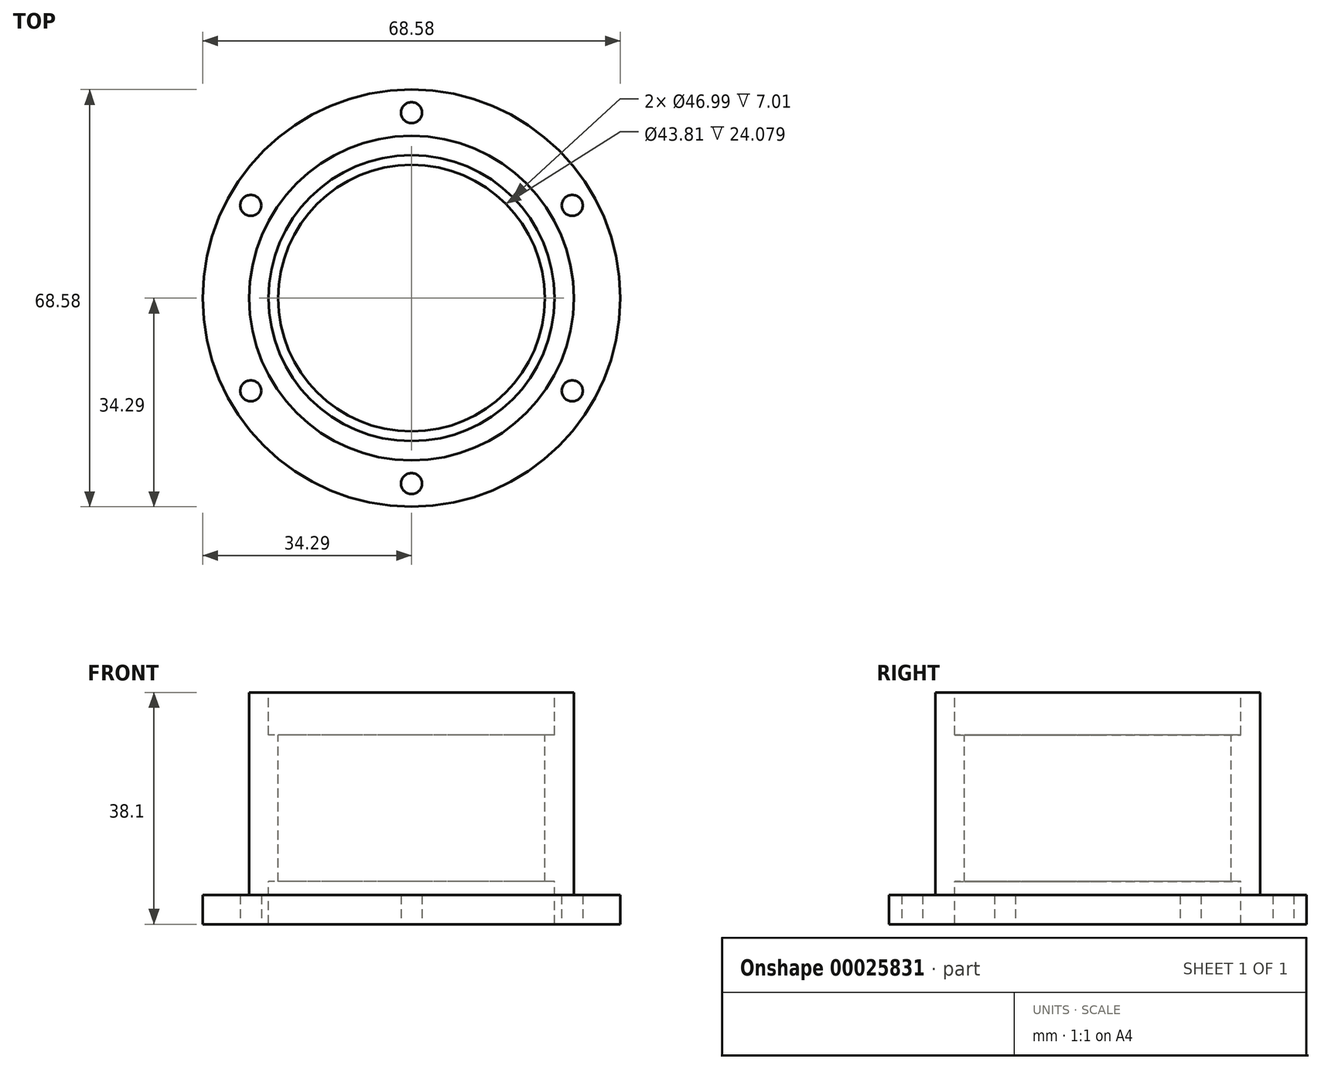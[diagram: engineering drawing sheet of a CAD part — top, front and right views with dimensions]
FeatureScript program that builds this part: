
annotation { "Feature Type Name" : "Feature", "Feature Type Description" : "" }
export const myFeature = defineFeature(function(context is Context, id is Id, definition is map)
    precondition{}
    {
        {
            var Q0;
            Q0=qCreatedBy(makeId("Front.planeOp"),FACE);
            var sketch = newSketch(context, id + "F0", { "sketchPlane" : qUnion([Q0])});
            skLineSegment(sketch, "E0", {"start": v(0, 31.7) * mm, "end": v(0, 0) * mm, "construction": true});
            skLineSegment(sketch, "E1", {"start": v(0, 0) * mm, "end": v(-23.5, 0) * mm, "construction": true});
            skLineSegment(sketch, "E2.bottom", {"start": v(-23.5, 0) * mm, "end": v(-34.3, 0) * mm});
            skLineSegment(sketch, "E2.top", {"start": v(-23.5, 38.1) * mm, "end": v(-26.67, 38.1) * mm});
            skLineSegment(sketch, "E2.left", {"start": v(-23.5, 0) * mm, "end": v(-23.5, 7.01) * mm});
            skLineSegment(sketch, "E2.right", {"start": v(-34.3, 0) * mm, "end": v(-34.3, 4.78) * mm});
            skLineSegment(sketch, "E3.bottom", {"start": v(-23.5, 31.09) * mm, "end": v(-21.9, 31.09) * mm});
            skLineSegment(sketch, "E3.top", {"start": v(-23.5, 7.01) * mm, "end": v(-21.9, 7.01) * mm});
            skLineSegment(sketch, "E3.right", {"start": v(-21.9, 31.09) * mm, "end": v(-21.9, 7.01) * mm});
            skLineSegment(sketch, "E4.bottom", {"start": v(-26.67, 4.78) * mm, "end": v(-34.3, 4.78) * mm});
            skLineSegment(sketch, "E4.left", {"start": v(-26.67, 4.78) * mm, "end": v(-26.67, 38.1) * mm});
            skLineSegment(sketch, "E5.trimOffspring", {"start": v(-23.5, 31.09) * mm, "end": v(-23.5, 38.1) * mm});
            skSolve(sketch);
        }
        {
            var Q0;
            Q0=makeQuery(id+"F0.imprint","IMPRINT",FACE,{"disambiguationData":[TD([[makeQuery(id+"F0.imprint","IMPRINT",EDGE,{"derivedFrom":sQuery(id+"F0.wireOp",EDGE,"E2.bottom")}),-1.0]])]});
            var Q1;
            Q1=sQuery(id+"F0.wireOp",EDGE,"E0");
            revolve(context, id + "F1", {"entities" : qUnion([Q0]), "axis" : qUnion([Q1]), "revolveType" : RevolveType.FULL});
        }
        {
            var Q0;
            Q0=makeQuery(id+"F1.opRevolve","SWEPT_FACE",FACE,{"disambiguationData":[OSD([sQuery(id+"F0.wireOp",EDGE,"E2.bottom")])]});
            var sketch = newSketch(context, id + "F2", { "sketchPlane" : qUnion([Q0])});
            skLineSegment(sketch, "E6", {"start": v(0, 0) * mm, "end": v(0, 30.48) * mm});
            skLineSegment(sketch, "E7.1.0", {"start": v(0, 0) * mm, "end": v(-26.4, 15.24) * mm});
            skLineSegment(sketch, "E7.2.0", {"start": v(0, 0) * mm, "end": v(-26.4, -15.24) * mm});
            skLineSegment(sketch, "E7.3.0", {"start": v(0, 0) * mm, "end": v(0, -30.48) * mm});
            skLineSegment(sketch, "E7.4.0", {"start": v(0, 0) * mm, "end": v(26.4, -15.24) * mm});
            skLineSegment(sketch, "E7.5.0", {"start": v(0, 0) * mm, "end": v(26.4, 15.24) * mm});
            skPoint(sketch, "E7.center", {"position": v(0, 0) * mm});
            skSolve(sketch);
        }
        {
            var Q0;
            Q0=sQuery(id+"F2.wireOp",VERTEX,"E6.end");
            var Q1;
            Q1=sQuery(id+"F2.wireOp",VERTEX,"E7.5.0.end");
            var Q2;
            Q2=sQuery(id+"F2.wireOp",VERTEX,"E7.4.0.end");
            var Q3;
            Q3=sQuery(id+"F2.wireOp",VERTEX,"E7.3.0.end");
            var Q4;
            Q4=sQuery(id+"F2.wireOp",VERTEX,"E7.2.0.end");
            var Q5;
            Q5=sQuery(id+"F2.wireOp",VERTEX,"E7.1.0.end");
            var Q6;
            Q6=makeQuery(id+"F1.opRevolve","SWEPT_BODY",BODY,{"disambiguationData":[OSD([sQuery(id+"F0.wireOp",EDGE,"E2.bottom"),sQuery(id+"F0.wireOp",EDGE,"E2.top"),sQuery(id+"F0.wireOp",EDGE,"E2.left"),sQuery(id+"F0.wireOp",EDGE,"E2.right"),sQuery(id+"F0.wireOp",EDGE,"E3.bottom"),sQuery(id+"F0.wireOp",EDGE,"E3.top"),sQuery(id+"F0.wireOp",EDGE,"E3.right"),sQuery(id+"F0.wireOp",EDGE,"E4.bottom"),sQuery(id+"F0.wireOp",EDGE,"E4.left"),sQuery(id+"F0.wireOp",EDGE,"E5.trimOffspring")])]});
            hole(context, id + "F3", {"style" : HoleStyle.SIMPLE, "holeDiameter" : 3.45 * mm, "endStyle" : HoleEndStyle.THROUGH, "locations" : qUnion([Q0, Q1, Q2, Q3, Q4, Q5]), "scope" : qUnion([Q6])});
        }
    });
